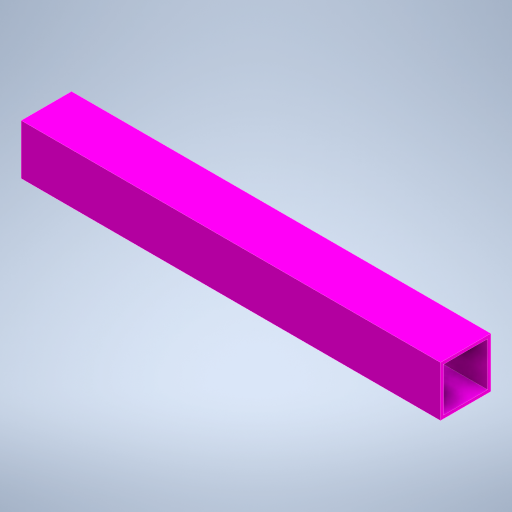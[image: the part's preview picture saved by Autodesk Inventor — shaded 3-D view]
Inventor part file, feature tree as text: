
AUTODESK INVENTOR PART (.ipt)
format: ipt  version: 2024 (Build 280153000, 153)  size: 220,672 bytes
history: native  units: in
note: dims shown in document units (in); Inventor stores cm internally (conversion verified against a paired STEP export)
features: extrude x1, sketch x1
ambient origin geometry x8: Origin, YZ Plane, XZ Plane, XY Plane, X Axis, Y Axis, Z Axis, Center Point
bodies: Solid1 (feature_tree)
feature tree (2):
  extrude  "Extrusion1"  Depth=1.0in
  sketch  "Sketch1"  dims[d0=1.0in d1=1.0in d2=0.0625in d3=8.34in d4=0.0in]
